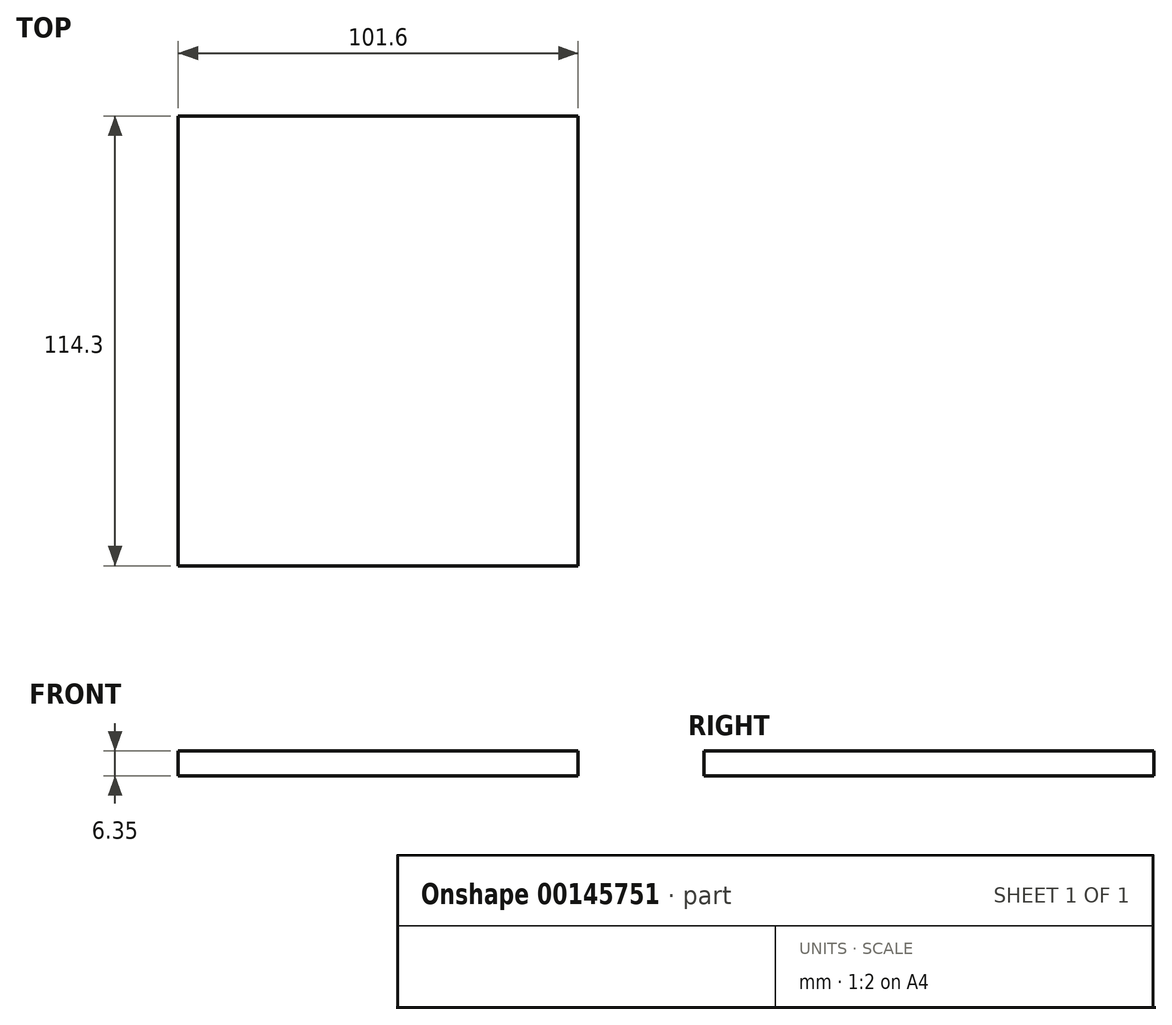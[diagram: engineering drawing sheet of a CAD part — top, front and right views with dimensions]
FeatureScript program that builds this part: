
annotation { "Feature Type Name" : "Feature", "Feature Type Description" : "" }
export const myFeature = defineFeature(function(context is Context, id is Id, definition is map)
    precondition{}
    {
        {
            var Q0;
            Q0=qCreatedBy(makeId("Top.planeOp"),FACE);
            var sketch = newSketch(context, id + "F0", { "sketchPlane" : qUnion([Q0])});
            skLineSegment(sketch, "E0.bottom", {"start": v(50.8, 57.15) * mm, "end": v(-50.8, 57.15) * mm});
            skLineSegment(sketch, "E0.top", {"start": v(50.8, -57.15) * mm, "end": v(-50.8, -57.15) * mm});
            skLineSegment(sketch, "E0.left", {"start": v(50.8, 57.15) * mm, "end": v(50.8, -57.15) * mm});
            skLineSegment(sketch, "E0.right", {"start": v(-50.8, 57.15) * mm, "end": v(-50.8, -57.15) * mm});
            skPoint(sketch, "E0.middle", {"position": v(0, 0) * mm});
            skSolve(sketch);
        }
        {
            var Q0;
            Q0 = qSketchRegion(id + "F0", true);
            extrude(context, id + "F1", {"entities" : qUnion([Q0]), "depth" : 6.35 * mm});
        }
    });
